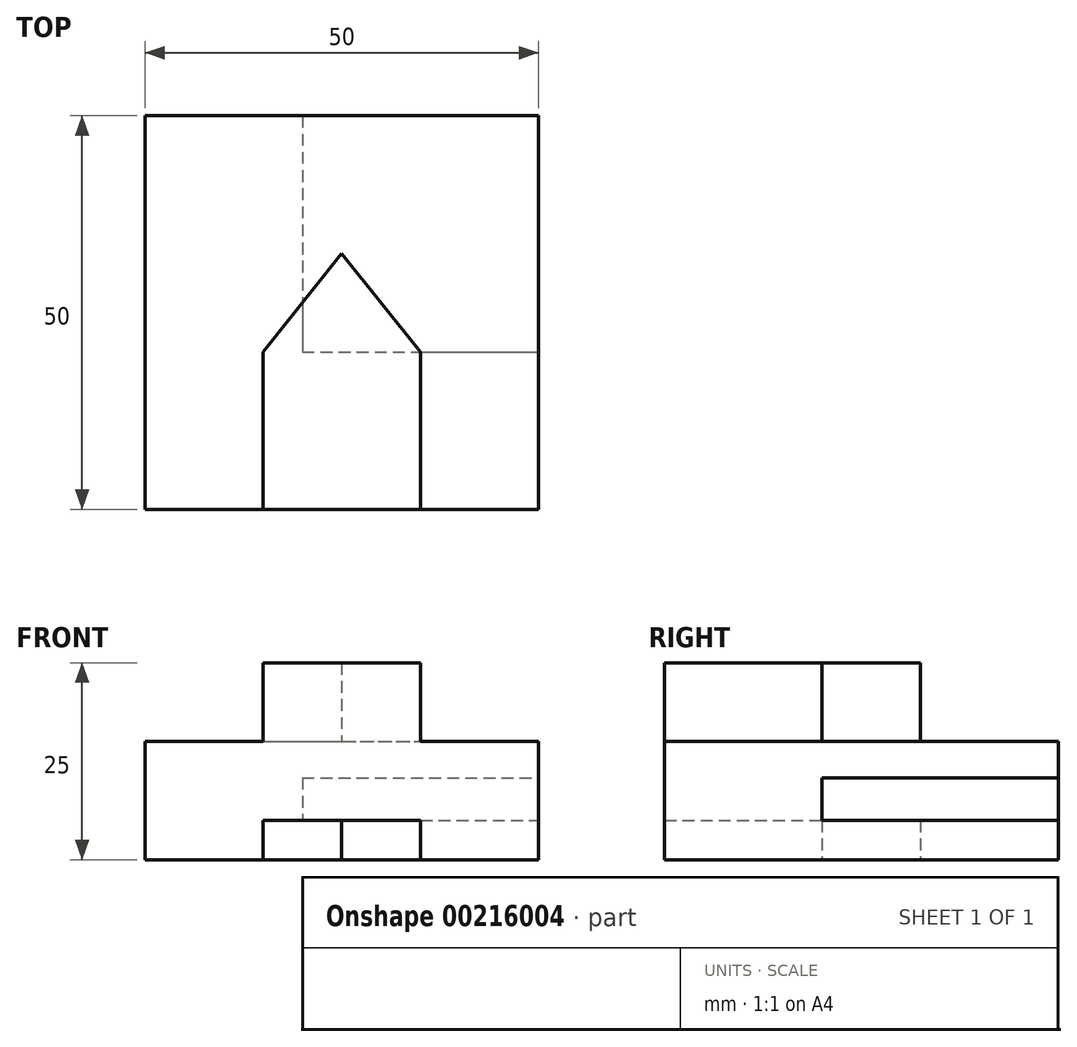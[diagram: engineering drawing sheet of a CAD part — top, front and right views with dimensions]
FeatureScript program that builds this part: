
annotation { "Feature Type Name" : "Feature", "Feature Type Description" : "" }
export const myFeature = defineFeature(function(context is Context, id is Id, definition is map)
    precondition{}
    {
        {
            var Q0;
            Q0=qCreatedBy(makeId("Top.planeOp"),FACE);
            var sketch = newSketch(context, id + "F0", { "sketchPlane" : qUnion([Q0])});
            skLineSegment(sketch, "E0.bottom", {"start": v(0, 0) * mm, "end": v(50, 0) * mm});
            skLineSegment(sketch, "E0.top", {"start": v(0, -50) * mm, "end": v(50, -50) * mm});
            skLineSegment(sketch, "E0.left", {"start": v(0, 0) * mm, "end": v(0, -50) * mm});
            skLineSegment(sketch, "E0.right", {"start": v(50, 0) * mm, "end": v(50, -50) * mm});
            skSolve(sketch);
        }
        {
            var Q0;
            Q0=makeQuery(id+"F0.imprint","IMPRINT",FACE,{"disambiguationData":[TD([[makeQuery(id+"F0.imprint","IMPRINT",EDGE,{"derivedFrom":sQuery(id+"F0.wireOp",EDGE,"E0.bottom")}),-1.0]])]});
            extrude(context, id + "F1", {"entities" : qUnion([Q0]), "depth" : 15 * mm});
        }
        {
            var Q0;
            Q0=makeQuery(id+"F1.opExtrude","CAP_FACE",FACE,{"disambiguationData":[OSD([sQuery(id+"F0.wireOp",EDGE,"E0.bottom"),sQuery(id+"F0.wireOp",EDGE,"E0.top"),sQuery(id+"F0.wireOp",EDGE,"E0.left"),sQuery(id+"F0.wireOp",EDGE,"E0.right")])],"isStart":false});
            var sketch = newSketch(context, id + "F2", { "sketchPlane" : qUnion([Q0])});
            skLineSegment(sketch, "E1.bottom", {"start": v(15, -50) * mm, "end": v(35, -50) * mm});
            skLineSegment(sketch, "E1.left", {"start": v(15, -50) * mm, "end": v(15, -30) * mm});
            skLineSegment(sketch, "E1.right", {"start": v(35, -50) * mm, "end": v(35, -30) * mm});
            skLineSegment(sketch, "E2", {"start": v(15, -30) * mm, "end": v(25, -17.51) * mm});
            skLineSegment(sketch, "E3", {"start": v(25, -17.51) * mm, "end": v(35, -30) * mm});
            skSolve(sketch);
        }
        {
            var Q0;
            Q0=qSketchRegion(id+"F2",true);
            extrude(context, id + "F3", {"entities" : qUnion([Q0]), "operationType" : NewBodyOperationType.ADD, "offsetDistance" : 25 * mm, "depth" : 10 * mm});
        }
        {
            var Q0;
            Q0=makeQuery(id+"F1.opExtrude","CAP_FACE",FACE,{"disambiguationData":[OSD([sQuery(id+"F0.wireOp",EDGE,"E0.bottom"),sQuery(id+"F0.wireOp",EDGE,"E0.top"),sQuery(id+"F0.wireOp",EDGE,"E0.left"),sQuery(id+"F0.wireOp",EDGE,"E0.right")])],"isStart":true});
            var sketch = newSketch(context, id + "F4", { "sketchPlane" : qUnion([Q0])});
            skLineSegment(sketch, "E4.bottom", {"start": v(15, 50) * mm, "end": v(35, 50) * mm});
            skLineSegment(sketch, "E4.left", {"start": v(15, 50) * mm, "end": v(15, 30) * mm});
            skLineSegment(sketch, "E4.right", {"start": v(35, 50) * mm, "end": v(35, 30) * mm});
            skLineSegment(sketch, "E5", {"start": v(35, 30) * mm, "end": v(25, 17.51) * mm});
            skLineSegment(sketch, "E6", {"start": v(25, 17.51) * mm, "end": v(15, 30) * mm});
            skSolve(sketch);
        }
        {
            var Q0;
            Q0=qSketchRegion(id+"F4",true);
            extrude(context, id + "F5", {"entities" : qUnion([Q0]), "operationType" : NewBodyOperationType.REMOVE, "oppositeDirection" : true, "offsetDistance" : 25 * mm, "depth" : 5 * mm});
        }
        {
            var Q0;
            Q0=makeQuery(id+"F1.opExtrude","SWEPT_FACE",FACE,{"disambiguationData":[OSD([sQuery(id+"F0.wireOp",EDGE,"E0.right")])]});
            var sketch = newSketch(context, id + "F6", { "sketchPlane" : qUnion([Q0])});
            skLineSegment(sketch, "E7.bottom", {"start": v(0, 10.4) * mm, "end": v(-30, 10.4) * mm});
            skLineSegment(sketch, "E7.top", {"start": v(0, 5) * mm, "end": v(-30, 5) * mm});
            skLineSegment(sketch, "E7.left", {"start": v(0, 10.4) * mm, "end": v(0, 5) * mm});
            skLineSegment(sketch, "E7.right", {"start": v(-30, 10.4) * mm, "end": v(-30, 5) * mm});
            skSolve(sketch);
        }
        {
            var Q0;
            Q0=qSketchRegion(id+"F6",true);
            extrude(context, id + "F7", {"entities" : qUnion([Q0]), "operationType" : NewBodyOperationType.REMOVE, "oppositeDirection" : true, "depth" : 30 * mm});
        }
    });
